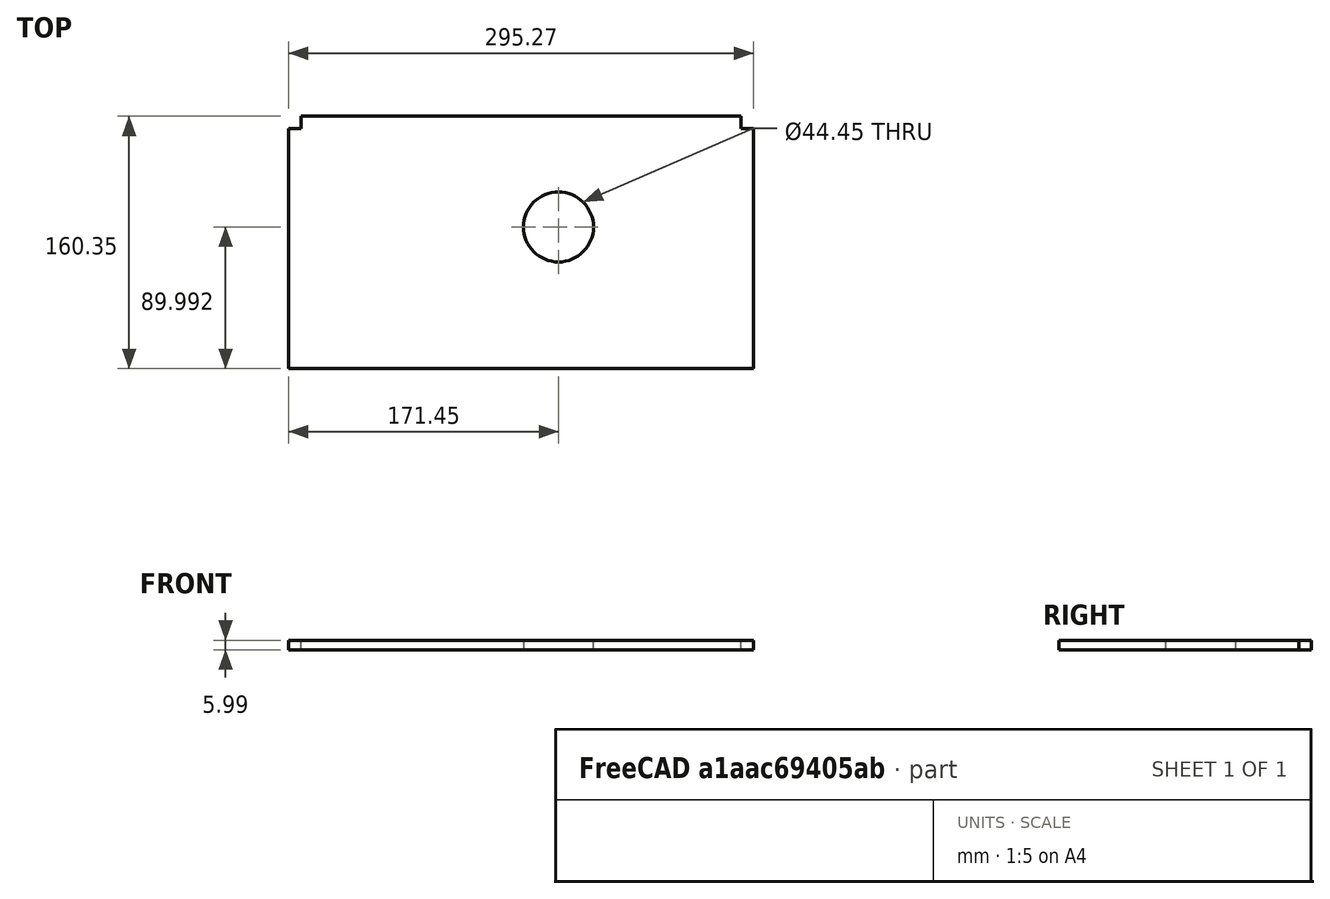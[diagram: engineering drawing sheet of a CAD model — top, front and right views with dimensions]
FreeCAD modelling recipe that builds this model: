
FCSTD DOCUMENT  (FreeCAD 0.19R24267 (Git))
Label: Inv2-P10
License: All rights reserved
LicenseURL: http://en.wikipedia.org/wiki/All_rights_reserved
objects: TechDraw::DrawViewDimension×10, TechDraw::DrawProjGroupItem×2, TechDraw::DrawHatch×2, TechDraw::DrawViewAnnotation×2, Sketcher::SketchObject×1, Part::Extrusion×1, TechDraw::DrawSVGTemplate×1, TechDraw::DrawProjGroup×1, TechDraw::DrawPage×1
note: 2 computed .brp shape members not serialized (recipe doc carries the construction recipe); baked Part::Feature solids carry a one-line shape summary decoded from their .brp

FEATURE [Sketcher::SketchObject] Sketch
  FullyConstrained = true
  sketch-geometry (9):
    g0: LineSegment StartX=0 StartY=0 StartZ=0 EndX=295.275 EndY=0 EndZ=0
    g1: LineSegment StartX=295.275 StartY=0 StartZ=0 EndX=295.275 EndY=152.4 EndZ=0
    g2: LineSegment StartX=295.275 StartY=152.4 StartZ=0 EndX=287.325 EndY=152.4 EndZ=0
    g3: LineSegment StartX=287.325 StartY=152.4 StartZ=0 EndX=287.325 EndY=160.35 EndZ=0
    g4: LineSegment StartX=287.325 StartY=160.35 StartZ=0 EndX=7.9502 EndY=160.35 EndZ=0
    g5: LineSegment StartX=7.9502 StartY=160.35 StartZ=0 EndX=7.9502 EndY=152.4 EndZ=0
    g6: LineSegment StartX=7.9502 StartY=152.4 StartZ=0 EndX=0 EndY=152.4 EndZ=0
    g7: LineSegment StartX=0 StartY=152.4 StartZ=0 EndX=0 EndY=0 EndZ=0
    g8: Circle CenterX=171.45 CenterY=89.9922 CenterZ=0 NormalX=0 NormalY=0 NormalZ=1 AngleXU=0 Radius=22.225
  constraints (26):
    c: Coincident(g0,g-1)
    c: Coincident(g1,g0)
    c: Vertical(g1)
    c: Coincident(g2,g1)
    c: Coincident(g3,g2)
    c: Coincident(g4,g3)
    c: Horizontal(g4)
    c: Coincident(g5,g4)
    c: Coincident(g6,g5)
    c: Horizontal(g6)
    c: Coincident(g7,g6)
    c: Coincident(g7,g0)
    c: Vertical(g7)
    c: Vertical(g5)
    c: Horizontal(g2)
    c: Vertical(g3)
    c: Horizontal(g0)
    c: DistanceX(g0,g0) = 295.275
    c: DistanceX(g6,g6) = 7.9502
    c: Equal(g6,g5)
    c: Equal(g6,g3)
    c: Equal(g2,g6)
    c: Distance(g4,g0) = 160.35
    c: Distance(g8,g0) = 89.9922
    c: Distance(g8,g1) = 123.825
    c: Diameter(g8) = 44.45
FEATURE [Part::Extrusion] Extrude
  Base = -> Sketch
  Dir = (0,0,1)
  DirMode = 2
  FaceMakerClass = Part::FaceMakerBullseye
  LengthFwd = 5.9944
  LengthRev = 0
  Solid = true
  Symmetric = false
FEATURE [TechDraw::DrawSVGTemplate] Template
  Height = 215.9
  Orientation = 1
  Width = 279.4
FEATURE [TechDraw::DrawProjGroupItem] ProjItem  label="Front"
  CoarseView = false
  Direction = (0,0,1)
  Focus = 100
  HardHidden = false
  IsoCount = 0
  IsoHidden = false
  IsoVisible = false
  LockPosition = true
  Perspective = false
  Rotation = 0
  RotationVector = (1,0,0)
  Scale = 0.5
  ScaleType = 2
  SeamHidden = false
  SeamVisible = true
  SmoothHidden = false
  SmoothVisible = true
  Source = -> [Extrude]
  Type = 0
  X = 0
  XDirection = (1,0,0)
  Y = 0
FEATURE [TechDraw::DrawProjGroupItem] ProjItem001  label="Left"
  CoarseView = false
  Direction = (-1,0,1e-16)
  Focus = 100
  HardHidden = false
  IsoCount = 0
  IsoHidden = false
  IsoVisible = false
  LockPosition = false
  Perspective = false
  Rotation = 0
  RotationVector = (1,0,0)
  Scale = 0.5
  ScaleType = 2
  SeamHidden = false
  SeamVisible = true
  SmoothHidden = false
  SmoothVisible = true
  Source = -> [Extrude]
  Type = 1
  X = 117.161
  XDirection = (1e-16,0,1)
  Y = 0
FEATURE [TechDraw::DrawProjGroup] ProjGroup
  Anchor = -> ProjItem
  AutoDistribute = true
  LockPosition = false
  ProjectionType = 0
  Rotation = 0
  Scale = 0.5
  ScaleType = 2
  Source = -> [Extrude]
  Views = -> [ProjItem,ProjItem001]
  X = 122.864
  Y = 104.042
  spacingX = 15.0114
  spacingY = 15.0114
FEATURE [TechDraw::DrawHatch] Hatch  label="HatchF0"
  HatchPattern = <path>
  Source = -> ProjItem [Face0]
FEATURE [TechDraw::DrawHatch] Hatch001  label="Hatch001F1"
  HatchPattern = <path>
  Source = -> ProjItem001 [Face1,Face2]
FEATURE [TechDraw::DrawViewDimension] Dimension
  Arbitrary = false
  ArbitraryTolerances = false
  EqualTolerance = true
  FormatSpec = %.3f
  FormatSpecOverTolerance = %+.3f
  FormatSpecUnderTolerance = %+.3f
  Inverted = false
  LockPosition = false
  MeasureType = 1
  OverTolerance = 0
  References2D = -> [ProjItem]
  Rotation = 0
  ScaleType = 0
  TheoreticalExact = false
  Type = 2
  UnderTolerance = 0
  X = 94.1077
  Y = 1.47372
FEATURE [TechDraw::DrawViewDimension] Dimension001
  Arbitrary = false
  ArbitraryTolerances = false
  EqualTolerance = true
  FormatSpec = %.3f
  FormatSpecOverTolerance = %+.3f
  FormatSpecUnderTolerance = %+.3f
  Inverted = false
  LockPosition = false
  MeasureType = 1
  OverTolerance = 0
  References2D = -> [ProjItem001]
  Rotation = 0
  ScaleType = 0
  TheoreticalExact = false
  Type = 1
  UnderTolerance = 0
  X = 16.8292
  Y = 21.4838
FEATURE [TechDraw::DrawViewDimension] Dimension002
  Arbitrary = false
  ArbitraryTolerances = false
  EqualTolerance = true
  FormatSpec = %.3f
  FormatSpecOverTolerance = %+.3f
  FormatSpecUnderTolerance = %+.3f
  Inverted = false
  LockPosition = false
  MeasureType = 1
  OverTolerance = 0
  References2D = -> [ProjItem]
  Rotation = 0
  ScaleType = 0
  TheoreticalExact = false
  Type = 1
  UnderTolerance = 0
  X = -1.45294
  Y = -52.1954
FEATURE [TechDraw::DrawViewDimension] Dimension003
  Arbitrary = false
  ArbitraryTolerances = false
  EqualTolerance = true
  FormatSpec = %.3f
  FormatSpecOverTolerance = %+.3f
  FormatSpecUnderTolerance = %+.3f
  Inverted = false
  LockPosition = false
  MeasureType = 1
  OverTolerance = 0
  References2D = -> [ProjItem]
  Rotation = 0
  ScaleType = 0
  TheoreticalExact = false
  Type = 1
  UnderTolerance = 0
  X = -87.2298
  Y = 30.2136
FEATURE [TechDraw::DrawViewDimension] Dimension004
  Arbitrary = false
  ArbitraryTolerances = false
  EqualTolerance = true
  FormatSpec = %.3f
  FormatSpecOverTolerance = %+.3f
  FormatSpecUnderTolerance = %+.3f
  Inverted = false
  LockPosition = false
  MeasureType = 1
  OverTolerance = 0
  References2D = -> [ProjItem]
  Rotation = 0
  ScaleType = 0
  TheoreticalExact = false
  Type = 2
  UnderTolerance = 0
  X = -60.8888
  Y = 56.0098
FEATURE [TechDraw::DrawViewDimension] Dimension005
  Arbitrary = false
  ArbitraryTolerances = false
  EqualTolerance = true
  FormatSpec = %.3f
  FormatSpecOverTolerance = %+.3f
  FormatSpecUnderTolerance = %+.3f
  Inverted = false
  LockPosition = false
  MeasureType = 1
  OverTolerance = 0
  References2D = -> [ProjItem]
  Rotation = 0
  ScaleType = 0
  TheoreticalExact = false
  Type = 2
  UnderTolerance = 0
  X = 53.6274
  Y = 57.6088
FEATURE [TechDraw::DrawViewDimension] Dimension006
  Arbitrary = false
  ArbitraryTolerances = false
  EqualTolerance = true
  FormatSpec = %.3f
  FormatSpecOverTolerance = %+.3f
  FormatSpecUnderTolerance = %+.3f
  Inverted = false
  LockPosition = false
  MeasureType = 1
  OverTolerance = 0
  References2D = -> [ProjItem]
  Rotation = 0
  ScaleType = 0
  TheoreticalExact = false
  Type = 1
  UnderTolerance = 0
  X = 87.1452
  Y = 29.0059
FEATURE [TechDraw::DrawViewDimension] Dimension007
  Arbitrary = false
  ArbitraryTolerances = false
  EqualTolerance = true
  FormatSpec = ⌀%.3f
  FormatSpecOverTolerance = %+.3f
  FormatSpecUnderTolerance = %+.3f
  Inverted = false
  LockPosition = false
  MeasureType = 1
  OverTolerance = 0
  References2D = -> [ProjItem]
  Rotation = 0
  ScaleType = 0
  TheoreticalExact = false
  Type = 5
  UnderTolerance = 0
  X = -10.8152
  Y = -10.5647
FEATURE [TechDraw::DrawViewDimension] Dimension008
  Arbitrary = false
  ArbitraryTolerances = false
  EqualTolerance = true
  FormatSpec = %.3f
  FormatSpecOverTolerance = %+.3f
  FormatSpecUnderTolerance = %+.3f
  Inverted = false
  LockPosition = false
  MeasureType = 1
  OverTolerance = 0
  References2D = -> [ProjItem]
  Rotation = 0
  ScaleType = 0
  TheoreticalExact = false
  Type = 2
  UnderTolerance = 0
  X = 28.9665
  Y = -19.2932
FEATURE [TechDraw::DrawViewDimension] Dimension009
  Arbitrary = false
  ArbitraryTolerances = false
  EqualTolerance = true
  FormatSpec = %.3f
  FormatSpecOverTolerance = %+.3f
  FormatSpecUnderTolerance = %+.3f
  Inverted = false
  LockPosition = false
  MeasureType = 1
  OverTolerance = 0
  References2D = -> [ProjItem]
  Rotation = 0
  ScaleType = 0
  TheoreticalExact = false
  Type = 1
  UnderTolerance = 0
  X = -22.6647
  Y = 23.1204
FEATURE [TechDraw::DrawViewAnnotation] Annotation
  Font = osifont
  LineSpace = 80
  LockPosition = false
  MaxWidth = -1
  Rotation = 0
  ScaleType = 0
  Text = Figure S2 (Inverted 2) | Panel 10 [camera side] | Quantity: 1
  TextSize = 5.0038
  TextStyle = 0
  X = 33.3133
  Y = 195.58
FEATURE [TechDraw::DrawViewAnnotation] Annotation002
  Font = osifont
  LineSpace = 80
  LockPosition = false
  MaxWidth = -1
  Rotation = 0
  ScaleType = 0
  Text = Units: Inches
  TextSize = 5.0038
  TextStyle = 0
  X = 259.08
  Y = 5.08
FEATURE [TechDraw::DrawPage] Page
  KeepUpdated = true
  NextBalloonIndex = 1
  ProjectionType = 0
  Template = -> Template
  Views = -> [ProjGroup,Dimension,Dimension001,Dimension002,Dimension003,Dimension004,Dimension005,Dimension006,Dimension007,Dimension008,Dimension009,Annotation,Annotation002]
note: 2 file-system paths scrubbed to <path> (originals preserved in the JSON sidecar)
